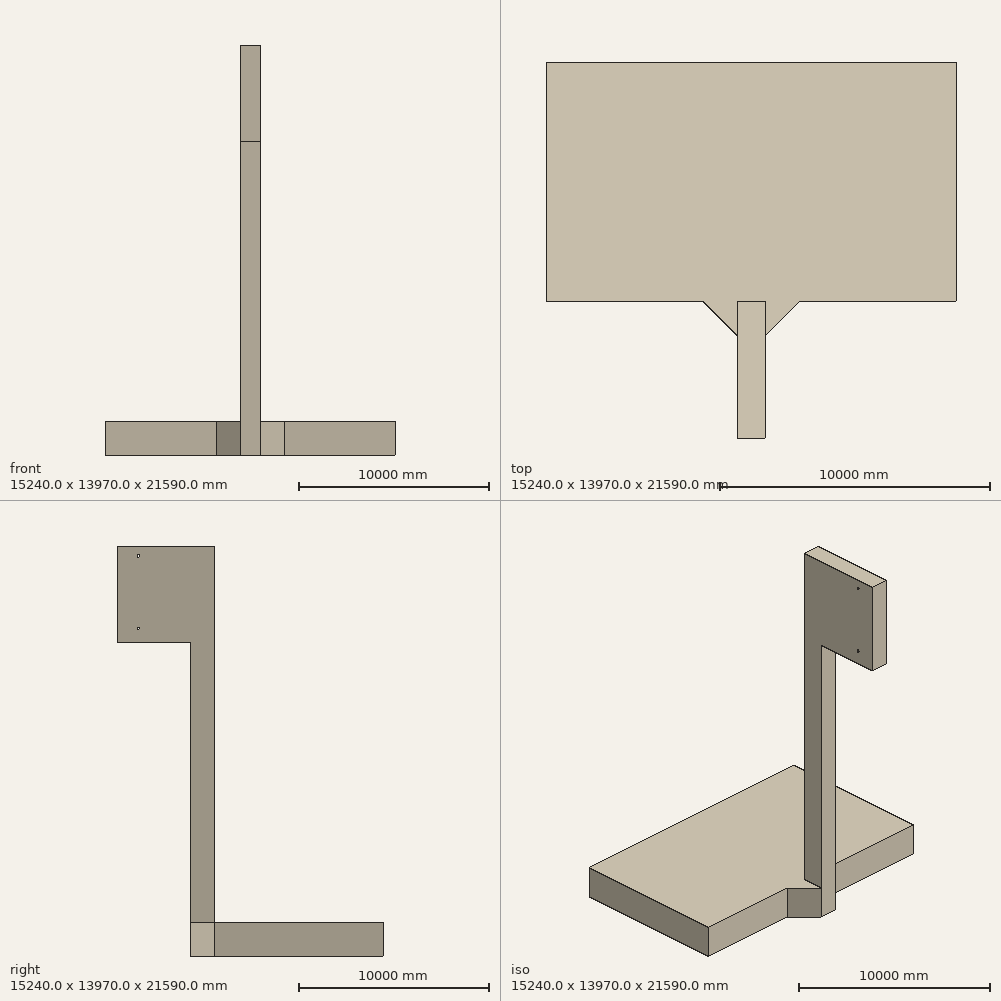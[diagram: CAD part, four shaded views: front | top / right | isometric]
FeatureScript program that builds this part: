
annotation { "Feature Type Name" : "Feature", "Feature Type Description" : "" }
export const myFeature = defineFeature(function(context is Context, id is Id, definition is map)
    precondition{}
    {
        {
            var Q0;
            Q0=qCreatedBy(makeId("Right.planeOp"),FACE);
            var sketch = newSketch(context, id + "F0", { "sketchPlane" : qUnion([Q0])});
            skLineSegment(sketch, "E0.bottom", {"start": v(0, 0) * mm, "end": v(5080, 0) * mm});
            skLineSegment(sketch, "E0.top", {"start": v(0, 5080) * mm, "end": v(5080, 5080) * mm});
            skLineSegment(sketch, "E0.left", {"start": v(0, 0) * mm, "end": v(0, 5080) * mm});
            skLineSegment(sketch, "E0.right", {"start": v(5080, 0) * mm, "end": v(5080, 5080) * mm});
            skSolve(sketch);
        }
        {
            var Q0;
            Q0=makeQuery(id+"F0.imprint","IMPRINT",FACE,{"disambiguationData":[TD([[makeQuery(id+"F0.imprint","IMPRINT",EDGE,{"derivedFrom":sQuery(id+"F0.wireOp",EDGE,"E0.bottom")}),1.0]])]});
            extrude(context, id + "F1", {"entities" : qUnion([Q0]), "depth" : 1016 * mm});
        }
        {
            var Q0;
            Q0=makeQuery(id+"F1.opExtrude","SWEPT_FACE",FACE,{"disambiguationData":[OSD([sQuery(id+"F0.wireOp",EDGE,"E0.bottom")])]});
            var sketch = newSketch(context, id + "F2", { "sketchPlane" : qUnion([Q0])});
            skLineSegment(sketch, "E1.bottom", {"start": v(1016, -5080) * mm, "end": v(0, -5080) * mm});
            skLineSegment(sketch, "E1.top", {"start": v(1016, -3810) * mm, "end": v(0, -3810) * mm});
            skLineSegment(sketch, "E1.left", {"start": v(1016, -5080) * mm, "end": v(1016, -3810) * mm});
            skLineSegment(sketch, "E1.right", {"start": v(0, -5080) * mm, "end": v(0, -3810) * mm});
            skSolve(sketch);
        }
        {
            var Q0;
            Q0=makeQuery(id+"F2.imprint","IMPRINT",FACE,{"disambiguationData":[TD([[makeQuery(id+"F2.imprint","IMPRINT",EDGE,{"derivedFrom":sQuery(id+"F2.wireOp",EDGE,"E1.bottom")}),-1.0]])]});
            extrude(context, id + "F3", {"entities" : qUnion([Q0]), "operationType" : NewBodyOperationType.ADD, "depth" : 16510 * mm});
        }
        {
            var Q0;
            Q0=makeQuery(id+"F3.boolean.opBoolean","MERGE",FACE,{"derivedFrom":[makeQuery(id+"F1.opExtrude","SWEPT_FACE",FACE,{"disambiguationData":[OSD([sQuery(id+"F0.wireOp",EDGE,"E0.right")])]}),makeQuery(id+"F3.opExtrude","SWEPT_FACE",FACE,{"disambiguationData":[OSD([sQuery(id+"F2.wireOp",EDGE,"E1.bottom")])]})]});
            var sketch = newSketch(context, id + "F4", { "sketchPlane" : qUnion([Q0])});
            skPoint(sketch, "E2.firstSnap0", {"position": v(-508, -16510) * mm});
            skLineSegment(sketch, "E2.bottom", {"start": v(7112, -16510) * mm, "end": v(-8128, -16510) * mm});
            skLineSegment(sketch, "E2.top", {"start": v(7112, -14821.76) * mm, "end": v(-8128, -14821.76) * mm});
            skLineSegment(sketch, "E2.left", {"start": v(7112, -16510) * mm, "end": v(7112, -14821.76) * mm});
            skLineSegment(sketch, "E2.right", {"start": v(-8128, -16510) * mm, "end": v(-8128, -14821.76) * mm});
            skSolve(sketch);
        }
        {
            var Q0;
            {var subQ3=sQuery(id+"F4.wireOp",EDGE,"E2.right");Q0=makeQuery(id+"F4.imprint","IMPRINT",FACE,{"disambiguationData":[TD([[makeQuery(id+"F4.imprint","IMPRINT",EDGE,{"derivedFrom":subQ3}),-1.0]])]});}
            var Q1;
            {var subQ3=sQuery(id+"F4.wireOp",EDGE,"E2.left");Q1=makeQuery(id+"F4.imprint","IMPRINT",FACE,{"disambiguationData":[TD([[makeQuery(id+"F4.imprint","IMPRINT",EDGE,{"derivedFrom":subQ3}),1.0]])]});}
            var Q2;
            {var subQ0=sQuery(id+"F4.wireOp",EDGE,"E2.bottom");var subQ1=sQuery(id+"F2.wireOp",EDGE,"E1.bottom");var subQ2=sQuery(id+"F0.wireOp",EDGE,"E0.right");var subQ3=makeQuery(id+"F3.boolean.opBoolean","MERGE",EDGE,{"derivedFrom":[makeQuery(id+"F1.opExtrude","CAP_EDGE",EDGE,{"disambiguationData":[OSD([subQ2])],"isStart":true}),makeQuery(id+"F3.opExtrude","SWEPT_EDGE",EDGE,{"disambiguationData":[OSD([subQ1,sQuery(id+"F2.wireOp",EDGE,"E1.right")])]})]});var subQ4=makeQuery(id+"F4.imprint","INTERSECT",VERTEX,{"derivedFrom":[subQ3,subQ0]});var subQ5=makeQuery(id+"F3.boolean.opBoolean","MERGE",EDGE,{"derivedFrom":[makeQuery(id+"F1.opExtrude","CAP_EDGE",EDGE,{"disambiguationData":[OSD([subQ2])],"isStart":false}),makeQuery(id+"F3.opExtrude","SWEPT_EDGE",EDGE,{"disambiguationData":[OSD([subQ1,sQuery(id+"F2.wireOp",EDGE,"E1.left")])]})]});var subQ6=makeQuery(id+"F4.imprint","INTERSECT",VERTEX,{"derivedFrom":[subQ5,subQ0]});Q2=makeQuery(id+"F4.imprint","IMPRINT",FACE,{"disambiguationData":[TD([[makeQuery(id+"F4.imprint","IMPRINT",EDGE,{"disambiguationData":[TD([[subQ4,1.0],[subQ6,-1.0]])],"derivedFrom":subQ0}),1.0]])]});}
            extrude(context, id + "F5", {"entities" : qUnion([Q0, Q1, Q2]), "operationType" : NewBodyOperationType.ADD, "depth" : 1270 * mm});
        }
        {
            var Q0;
            Q0=makeQuery(id+"F5.opExtrude","CAP_FACE",FACE,{"disambiguationData":[OSD([sQuery(id+"F4.wireOp",EDGE,"E2.bottom"),sQuery(id+"F4.wireOp",EDGE,"E2.top"),sQuery(id+"F4.wireOp",EDGE,"E2.left"),sQuery(id+"F4.wireOp",EDGE,"E2.right")])],"isStart":false});
            var sketch = newSketch(context, id + "F6", { "sketchPlane" : qUnion([Q0])});
            skLineSegment(sketch, "E3.bottom", {"start": v(-8128, -16510) * mm, "end": v(-6604, -16510) * mm});
            skLineSegment(sketch, "E3.top", {"start": v(-8128, -14821.76) * mm, "end": v(-6604, -14821.76) * mm});
            skLineSegment(sketch, "E3.left", {"start": v(-8128, -16510) * mm, "end": v(-8128, -14821.76) * mm});
            skLineSegment(sketch, "E3.right", {"start": v(-6604, -16510) * mm, "end": v(-6604, -14821.76) * mm});
            skLineSegment(sketch, "E4.bottom", {"start": v(7112, -16510) * mm, "end": v(5588, -16510) * mm});
            skLineSegment(sketch, "E4.top", {"start": v(7112, -14821.76) * mm, "end": v(5588, -14821.76) * mm});
            skLineSegment(sketch, "E4.left", {"start": v(7112, -16510) * mm, "end": v(7112, -14821.76) * mm});
            skLineSegment(sketch, "E4.right", {"start": v(5588, -16510) * mm, "end": v(5588, -14821.76) * mm});
            skLineSegment(sketch, "E5.bottom", {"start": v(-1270, -14821.76) * mm, "end": v(254, -14821.76) * mm});
            skLineSegment(sketch, "E5.top", {"start": v(-1270, -16510) * mm, "end": v(254, -16510) * mm});
            skLineSegment(sketch, "E5.left", {"start": v(-1270, -14821.76) * mm, "end": v(-1270, -16510) * mm});
            skLineSegment(sketch, "E5.right", {"start": v(254, -14821.76) * mm, "end": v(254, -16510) * mm});
            skSolve(sketch);
        }
        {
            var Q0;
            Q0=makeQuery(id+"F6.imprint","IMPRINT",FACE,{"disambiguationData":[TD([[makeQuery(id+"F6.imprint","IMPRINT",EDGE,{"derivedFrom":sQuery(id+"F6.wireOp",EDGE,"E4.bottom")}),-1.0]])]});
            var Q1;
            Q1=makeQuery(id+"F6.imprint","IMPRINT",FACE,{"disambiguationData":[TD([[makeQuery(id+"F6.imprint","IMPRINT",EDGE,{"derivedFrom":sQuery(id+"F6.wireOp",EDGE,"wSiAzH70-vk2G-D1VU-7fXP-obYUxkdqaIpf.bottom")}),-1.0]])]});
            var Q2;
            Q2=makeQuery(id+"F6.imprint","IMPRINT",FACE,{"disambiguationData":[TD([[makeQuery(id+"F6.imprint","IMPRINT",EDGE,{"derivedFrom":sQuery(id+"F6.wireOp",EDGE,"E3.bottom")}),-1.0]])]});
            var Q3;
            Q3=makeQuery(id+"F6.imprint","IMPRINT",FACE,{"disambiguationData":[TD([[makeQuery(id+"F6.imprint","IMPRINT",EDGE,{"derivedFrom":sQuery(id+"F6.wireOp",EDGE,"E5.bottom")}),1.0]])]});
            extrude(context, id + "F7", {"entities" : qUnion([Q0, Q1, Q2, Q3]), "operationType" : NewBodyOperationType.ADD, "depth" : 7620 * mm});
        }
        {
            var Q0;
            Q0=makeQuery(id+"F3.boolean.opBoolean","MERGE",FACE,{"derivedFrom":[makeQuery(id+"F1.opExtrude","CAP_FACE",FACE,{"disambiguationData":[OSD([sQuery(id+"F0.wireOp",EDGE,"E0.bottom"),sQuery(id+"F0.wireOp",EDGE,"E0.top"),sQuery(id+"F0.wireOp",EDGE,"E0.left"),sQuery(id+"F0.wireOp",EDGE,"E0.right")])],"isStart":true}),makeQuery(id+"F3.opExtrude","SWEPT_FACE",FACE,{"disambiguationData":[OSD([sQuery(id+"F2.wireOp",EDGE,"E1.right")])]})]});
            var sketch = newSketch(context, id + "F8", { "sketchPlane" : qUnion([Q0])});
            skCircle(sketch, "E6", {"center": v(-1089.7, 4572) * mm, "radius": 76.2 * mm});
            skCircle(sketch, "E7", {"center": v(-1089.7, 762) * mm, "radius": 74.17 * mm});
            skSolve(sketch);
        }
        {
            var Q0;
            Q0=makeQuery(id+"F8.imprint","IMPRINT",FACE,{"disambiguationData":[TD([[makeQuery(id+"F8.imprint","IMPRINT",EDGE,{"derivedFrom":sQuery(id+"F8.wireOp",EDGE,"E6")}),1.0]])]});
            var Q1;
            Q1=makeQuery(id+"F8.imprint","IMPRINT",FACE,{"disambiguationData":[TD([[makeQuery(id+"F8.imprint","IMPRINT",EDGE,{"derivedFrom":sQuery(id+"F8.wireOp",EDGE,"E7")}),1.0]])]});
            extrude(context, id + "F9", {"entities" : qUnion([Q0, Q1]), "operationType" : NewBodyOperationType.REMOVE, "endBound" : BoundingType.THROUGH_ALL, "oppositeDirection" : true, "depth" : 25.4 * mm});
        }
        {
            var Q0;
            Q0=makeQuery(id+"F7.boolean.opBoolean","MERGE",FACE,{"derivedFrom":[makeQuery(id+"F5.opExtrude","SWEPT_FACE",FACE,{"disambiguationData":[OSD([sQuery(id+"F4.wireOp",EDGE,"E2.top")])]}),makeQuery(id+"F7.opExtrude","SWEPT_FACE",FACE,{"disambiguationData":[OSD([sQuery(id+"F6.wireOp",EDGE,"E3.top")])]}),makeQuery(id+"F7.opExtrude","SWEPT_FACE",FACE,{"disambiguationData":[OSD([sQuery(id+"F6.wireOp",EDGE,"E4.top")])]}),makeQuery(id+"F7.opExtrude","SWEPT_FACE",FACE,{"disambiguationData":[OSD([sQuery(id+"F6.wireOp",EDGE,"E5.bottom")])]})]});
            var sketch = newSketch(context, id + "F10", { "sketchPlane" : qUnion([Q0])});
            skLineSegment(sketch, "E8.bottom", {"start": v(8128, 5080) * mm, "end": v(-7112, 5080) * mm});
            skLineSegment(sketch, "E8.top", {"start": v(8128, 13970) * mm, "end": v(-7112, 13970) * mm});
            skLineSegment(sketch, "E8.left", {"start": v(8128, 5080) * mm, "end": v(8128, 13970) * mm});
            skLineSegment(sketch, "E8.right", {"start": v(-7112, 5080) * mm, "end": v(-7112, 13970) * mm});
            skSolve(sketch);
        }
        {
            var Q0;
            {var subQ8=sQuery(id+"F10.wireOp",EDGE,"E8.left");Q0=makeQuery(id+"F10.imprint","IMPRINT",FACE,{"disambiguationData":[TD([[makeQuery(id+"F10.imprint","IMPRINT",EDGE,{"derivedFrom":subQ8}),-1.0]])]});}
            var Q1;
            {var subQ1=sQuery(id+"F6.wireOp",EDGE,"E3.right");var subQ2=sQuery(id+"F6.wireOp",EDGE,"E3.top");var subQ3=sQuery(id+"F4.wireOp",EDGE,"E2.top");var subQ4=makeQuery(id+"F7.opExtrude","SWEPT_EDGE",EDGE,{"disambiguationData":[OSD([subQ3,subQ2,subQ1])]});Q1=makeQuery(id+"F10.imprint","IMPRINT",FACE,{"disambiguationData":[TD([[makeQuery(id+"F10.imprint","IMPRINT",EDGE,{"derivedFrom":subQ4}),-1.0]])]});}
            var Q2;
            {var subQ1=sQuery(id+"F6.wireOp",EDGE,"E4.right");var subQ2=sQuery(id+"F6.wireOp",EDGE,"E4.top");var subQ3=sQuery(id+"F4.wireOp",EDGE,"E2.top");var subQ4=makeQuery(id+"F7.opExtrude","SWEPT_EDGE",EDGE,{"disambiguationData":[OSD([subQ3,subQ2,subQ1])]});Q2=makeQuery(id+"F10.imprint","IMPRINT",FACE,{"disambiguationData":[TD([[makeQuery(id+"F10.imprint","IMPRINT",EDGE,{"derivedFrom":subQ4}),1.0]])]});}
            extrude(context, id + "F11", {"entities" : qUnion([Q0, Q1, Q2]), "operationType" : NewBodyOperationType.ADD, "depth" : 76.2 * mm});
        }
        {
            var Q0;
            {var subQ0=sQuery(id+"F2.wireOp",EDGE,"E1.left");var subQ1=sQuery(id+"F2.wireOp",EDGE,"E1.bottom");var subQ5=sQuery(id+"F0.wireOp",EDGE,"E0.right");var subQ7=sQuery(id+"F0.wireOp",EDGE,"E0.top");var subQ10=sQuery(id+"F4.wireOp",EDGE,"E2.bottom");var subQ12=makeQuery(id+"F3.boolean.opBoolean","MERGE",EDGE,{"derivedFrom":[makeQuery(id+"F1.opExtrude","CAP_EDGE",EDGE,{"disambiguationData":[OSD([subQ5])],"isStart":false}),makeQuery(id+"F3.opExtrude","SWEPT_EDGE",EDGE,{"disambiguationData":[OSD([subQ1,subQ0])]})]});Q0=makeQuery(id+"F11.boolean.opBoolean","MERGE",EDGE,{"derivedFrom":[makeQuery(id+"F5.boolean.opBoolean","SPLIT",EDGE,{"disambiguationData":[TD([makeQuery(id+"F1.opExtrude","SWEPT_FACE",FACE,{"disambiguationData":[OSD([subQ7])]})])],"derivedFrom":subQ12}),makeQuery(id+"F5.boolean.opBoolean","SPLIT",EDGE,{"disambiguationData":[TD([makeQuery(id+"F5.opExtrude","SWEPT_FACE",FACE,{"disambiguationData":[OSD([subQ10])]})])],"derivedFrom":subQ12})]});}
            chamfer(context, id + "F12", {"entities" : qUnion([Q0]), "width" : 1270 * mm, "tangentPropagation" : true});
        }
        {
            var Q0;
            {var subQ0=sQuery(id+"F0.wireOp",EDGE,"E0.right");var subQ2=sQuery(id+"F2.wireOp",EDGE,"E1.bottom");var subQ4=sQuery(id+"F2.wireOp",EDGE,"E1.right");var subQ7=sQuery(id+"F0.wireOp",EDGE,"E0.top");var subQ10=sQuery(id+"F4.wireOp",EDGE,"E2.bottom");var subQ12=makeQuery(id+"F3.boolean.opBoolean","MERGE",EDGE,{"derivedFrom":[makeQuery(id+"F1.opExtrude","CAP_EDGE",EDGE,{"disambiguationData":[OSD([subQ0])],"isStart":true}),makeQuery(id+"F3.opExtrude","SWEPT_EDGE",EDGE,{"disambiguationData":[OSD([subQ2,subQ4])]})]});Q0=makeQuery(id+"F11.boolean.opBoolean","MERGE",EDGE,{"derivedFrom":[makeQuery(id+"F5.boolean.opBoolean","SPLIT",EDGE,{"disambiguationData":[TD([makeQuery(id+"F1.opExtrude","SWEPT_FACE",FACE,{"disambiguationData":[OSD([subQ7])]})])],"derivedFrom":subQ12}),makeQuery(id+"F5.boolean.opBoolean","SPLIT",EDGE,{"disambiguationData":[TD([makeQuery(id+"F5.opExtrude","SWEPT_FACE",FACE,{"disambiguationData":[OSD([subQ10])]})])],"derivedFrom":subQ12})]});}
            chamfer(context, id + "F13", {"entities" : qUnion([Q0]), "width" : 1270 * mm, "tangentPropagation" : true});
        }
    });
